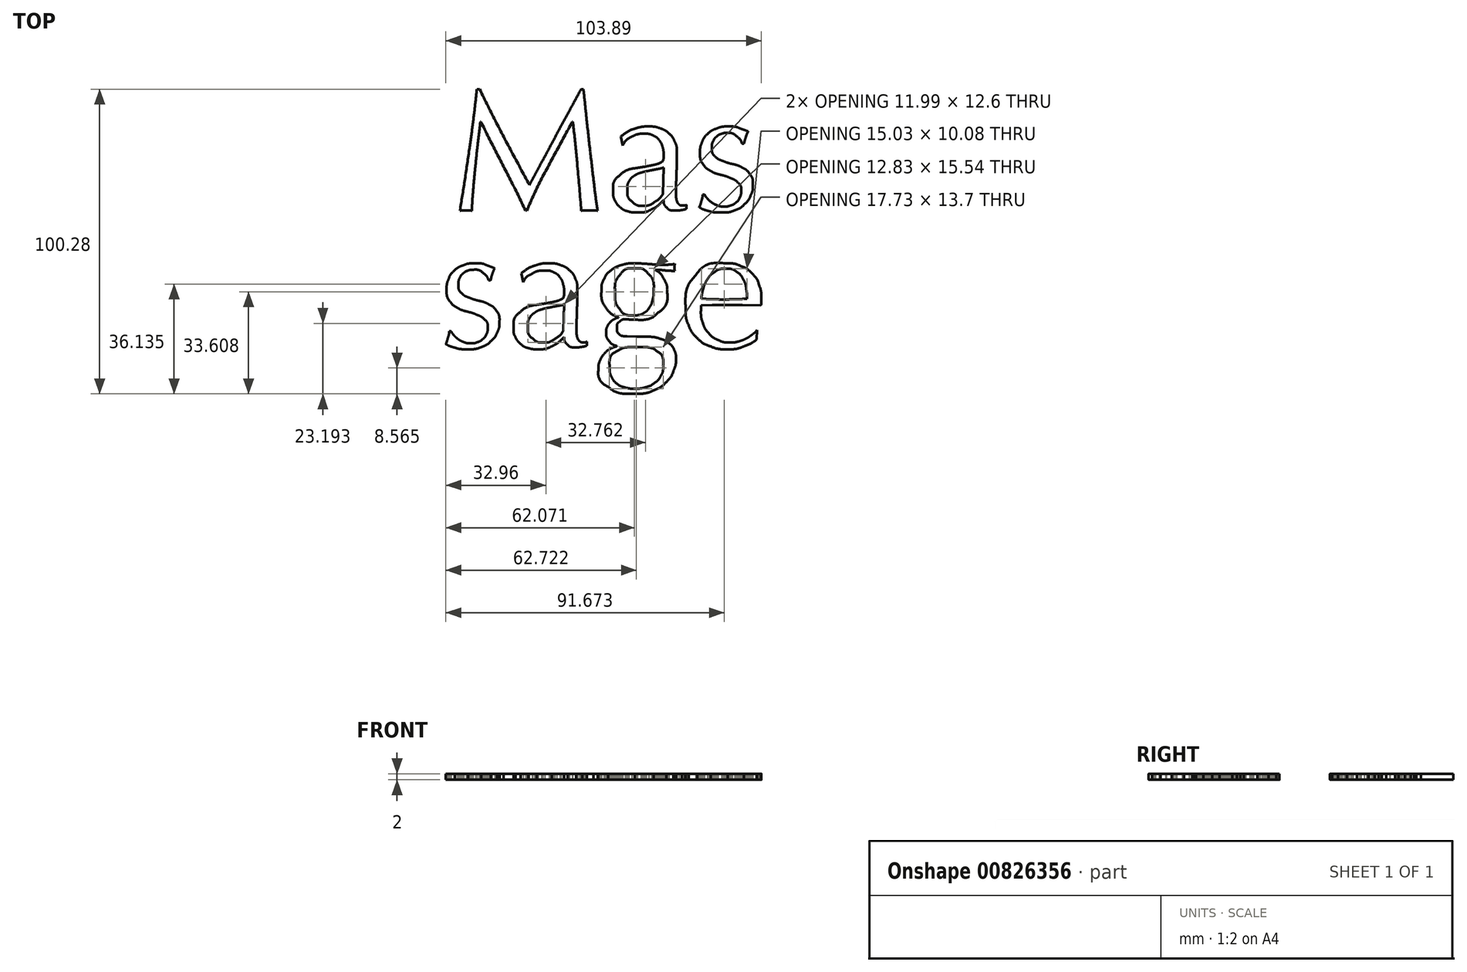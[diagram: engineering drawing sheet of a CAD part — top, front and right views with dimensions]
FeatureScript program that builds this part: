
annotation { "Feature Type Name" : "Feature", "Feature Type Description" : "" }
export const myFeature = defineFeature(function(context is Context, id is Id, definition is map)
    precondition{}
    {
        {
            var Q0;
            Q0=qCreatedBy(makeId("Top.planeOp"),FACE);
            var sketch = newSketch(context, id + "F0", { "sketchPlane" : qUnion([Q0])});
            skFitSpline(sketch, "E0", {"points": [v(-43.66, 49) * mm, v(-43.96, 45.94) * mm, v(-44.33, 42.72) * mm, v(-44.74, 39.33) * mm]});
            skFitSpline(sketch, "E1", {"points": [v(-44.74, 39.33) * mm, v(-45.16, 35.98) * mm, v(-45.62, 32.57) * mm, v(-46.12, 29.1) * mm]});
            skFitSpline(sketch, "E2", {"points": [v(-46.12, 29.1) * mm, v(-46.61, 25.64) * mm, v(-47.13, 22.2) * mm, v(-47.66, 18.76) * mm]});
            skFitSpline(sketch, "E3", {"points": [v(-47.66, 18.76) * mm, v(-48.2, 15.33) * mm, v(-48.7, 12.08) * mm, v(-49.2, 9) * mm]});
            skFitSpline(sketch, "E4", {"points": [v(-49.2, 9) * mm, v(-48.6, 9.07) * mm, v(-47.93, 9.1) * mm, v(-47.2, 9.1) * mm]});
            skFitSpline(sketch, "E5", {"points": [v(-47.2, 9.1) * mm, v(-46.48, 9.1) * mm, v(-45.81, 9.07) * mm, v(-45.2, 9) * mm]});
            skFitSpline(sketch, "E6", {"points": [v(-45.2, 9) * mm, v(-45.2, 10.51) * mm, v(-45.1, 12.46) * mm, v(-44.92, 14.82) * mm]});
            skFitSpline(sketch, "E7", {"points": [v(-44.92, 14.82) * mm, v(-44.73, 17.22) * mm, v(-44.5, 19.75) * mm, v(-44.23, 22.42) * mm]});
            skFitSpline(sketch, "E8", {"points": [v(-44.23, 22.42) * mm, v(-43.96, 25.12) * mm, v(-43.68, 27.85) * mm, v(-43.37, 30.6) * mm]});
            skFitSpline(sketch, "E9", {"points": [v(-43.37, 30.6) * mm, v(-43.03, 33.37) * mm, v(-42.73, 35.94) * mm, v(-42.46, 38.3) * mm]});
            skLineSegment(sketch, "E10", {"start": v(-42.69, 49) * mm, "end": v(-43.66, 49) * mm});
            skLineSegment(sketch, "E11", {"start": v(-43.66, 49) * mm, "end": v(-42.69, 49) * mm});
            skFitSpline(sketch, "E12", {"points": [v(-42.34, 38.3) * mm, v(-39.83, 33.28) * mm, v(-37.33, 28.34) * mm, v(-34.86, 23.5) * mm]});
            skFitSpline(sketch, "E13", {"points": [v(-34.86, 23.5) * mm, v(-32.34, 18.7) * mm, v(-29.94, 13.9) * mm, v(-27.66, 9.1) * mm]});
            skLineSegment(sketch, "E14", {"start": v(-42.46, 38.3) * mm, "end": v(-42.34, 38.3) * mm});
            skLineSegment(sketch, "E15", {"start": v(-42.34, 38.3) * mm, "end": v(-42.46, 38.3) * mm});
            skFitSpline(sketch, "E16", {"points": [v(-27.14, 9.1) * mm, v(-24.86, 14.29) * mm, v(-22.46, 19.24) * mm, v(-19.94, 23.96) * mm]});
            skFitSpline(sketch, "E17", {"points": [v(-19.94, 23.96) * mm, v(-17.4, 28.72) * mm, v(-14.8, 33.5) * mm, v(-12.17, 38.3) * mm]});
            skLineSegment(sketch, "E18", {"start": v(-27.66, 9.1) * mm, "end": v(-27.14, 9.1) * mm});
            skLineSegment(sketch, "E19", {"start": v(-27.14, 9.1) * mm, "end": v(-27.66, 9.1) * mm});
            skFitSpline(sketch, "E20", {"points": [v(-12.06, 38.3) * mm, v(-11.45, 33.35) * mm, v(-10.93, 28.5) * mm, v(-10.52, 23.73) * mm]});
            skFitSpline(sketch, "E21", {"points": [v(-10.52, 23.73) * mm, v(-10.1, 18.97) * mm, v(-9.68, 14.06) * mm, v(-9.26, 9) * mm]});
            skFitSpline(sketch, "E22", {"points": [v(-9.26, 9) * mm, v(-8.8, 9.07) * mm, v(-8.36, 9.1) * mm, v(-7.94, 9.1) * mm]});
            skFitSpline(sketch, "E23", {"points": [v(-7.94, 9.1) * mm, v(-7.49, 9.1) * mm, v(-7.03, 9.1) * mm, v(-6.57, 9.1) * mm]});
            skFitSpline(sketch, "E24", {"points": [v(-6.57, 9.1) * mm, v(-6.12, 9.1) * mm, v(-5.68, 9.1) * mm, v(-5.26, 9.1) * mm]});
            skFitSpline(sketch, "E25", {"points": [v(-5.26, 9.1) * mm, v(-4.8, 9.1) * mm, v(-4.34, 9.07) * mm, v(-3.89, 9) * mm]});
            skFitSpline(sketch, "E26", {"points": [v(-3.89, 9) * mm, v(-4.34, 12.15) * mm, v(-4.76, 15.33) * mm, v(-5.14, 18.53) * mm]});
            skFitSpline(sketch, "E27", {"points": [v(-5.14, 18.53) * mm, v(-5.53, 21.77) * mm, v(-5.9, 25.03) * mm, v(-6.29, 28.3) * mm]});
            skFitSpline(sketch, "E28", {"points": [v(-6.29, 28.3) * mm, v(-6.67, 31.62) * mm, v(-7.05, 34.97) * mm, v(-7.43, 38.36) * mm]});
            skFitSpline(sketch, "E29", {"points": [v(-7.43, 38.36) * mm, v(-7.77, 41.8) * mm, v(-8.15, 45.33) * mm, v(-8.57, 49) * mm]});
            skLineSegment(sketch, "E30", {"start": v(-12.17, 38.3) * mm, "end": v(-12.06, 38.3) * mm});
            skLineSegment(sketch, "E31", {"start": v(-12.06, 38.3) * mm, "end": v(-12.17, 38.3) * mm});
            skFitSpline(sketch, "E32", {"points": [v(-9.32, 49) * mm, v(-10.27, 47.24) * mm, v(-11.3, 45.35) * mm, v(-12.4, 43.33) * mm]});
            skFitSpline(sketch, "E33", {"points": [v(-12.4, 43.33) * mm, v(-13.5, 41.31) * mm, v(-14.63, 39.26) * mm, v(-15.77, 37.16) * mm]});
            skFitSpline(sketch, "E34", {"points": [v(-15.77, 37.16) * mm, v(-16.88, 35.07) * mm, v(-17.98, 33) * mm, v(-19.09, 30.93) * mm]});
            skFitSpline(sketch, "E35", {"points": [v(-19.09, 30.93) * mm, v(-20.15, 28.91) * mm, v(-21.16, 27.03) * mm, v(-22.12, 25.28) * mm]});
            skFitSpline(sketch, "E36", {"points": [v(-22.12, 25.28) * mm, v(-23.07, 23.52) * mm, v(-23.9, 21.96) * mm, v(-24.63, 20.6) * mm]});
            skFitSpline(sketch, "E37", {"points": [v(-24.63, 20.6) * mm, v(-25.35, 19.26) * mm, v(-25.9, 18.23) * mm, v(-26.29, 17.5) * mm]});
            skFitSpline(sketch, "E38", {"points": [v(-26.29, 17.5) * mm, v(-29.22, 22.88) * mm, v(-32.04, 28.11) * mm, v(-34.74, 33.22) * mm]});
            skFitSpline(sketch, "E39", {"points": [v(-34.74, 33.22) * mm, v(-37.41, 38.32) * mm, v(-40.06, 43.58) * mm, v(-42.69, 49) * mm]});
            skLineSegment(sketch, "E40", {"start": v(-8.57, 49) * mm, "end": v(-9.32, 49) * mm});
            skLineSegment(sketch, "E41", {"start": v(-9.32, 49) * mm, "end": v(-8.57, 49) * mm});
            skFitSpline(sketch, "E42", {"points": [v(17.64, 14.65) * mm, v(16.99, 13.58) * mm, v(16.06, 12.65) * mm, v(14.84, 11.85) * mm]});
            skFitSpline(sketch, "E43", {"points": [v(14.84, 11.85) * mm, v(13.66, 11.05) * mm, v(12.34, 10.65) * mm, v(10.9, 10.65) * mm]});
            skFitSpline(sketch, "E44", {"points": [v(10.9, 10.65) * mm, v(9.64, 10.65) * mm, v(8.5, 11.1) * mm, v(7.47, 12.02) * mm]});
            skFitSpline(sketch, "E45", {"points": [v(7.47, 12.02) * mm, v(6.44, 12.93) * mm, v(5.92, 14.29) * mm, v(5.92, 16.08) * mm]});
            skFitSpline(sketch, "E46", {"points": [v(5.92, 16.08) * mm, v(5.92, 17.14) * mm, v(6.11, 18.02) * mm, v(6.5, 18.7) * mm]});
            skFitSpline(sketch, "E47", {"points": [v(6.5, 18.7) * mm, v(6.91, 19.4) * mm, v(7.45, 19.96) * mm, v(8.1, 20.42) * mm]});
            skFitSpline(sketch, "E48", {"points": [v(8.1, 20.42) * mm, v(8.78, 20.88) * mm, v(9.54, 21.24) * mm, v(10.38, 21.5) * mm]});
            skFitSpline(sketch, "E49", {"points": [v(10.38, 21.5) * mm, v(11.26, 21.77) * mm, v(12.13, 21.98) * mm, v(13, 22.13) * mm]});
            skFitSpline(sketch, "E50", {"points": [v(13, 22.13) * mm, v(13.88, 22.32) * mm, v(14.74, 22.5) * mm, v(15.58, 22.65) * mm]});
            skFitSpline(sketch, "E51", {"points": [v(15.58, 22.65) * mm, v(16.46, 22.8) * mm, v(17.22, 23) * mm, v(17.87, 23.22) * mm]});
            skLineSegment(sketch, "E52", {"start": v(17.87, 23.22) * mm, "end": v(17.64, 14.65) * mm});
            skLineSegment(sketch, "E53", {"start": v(17.64, 14.65) * mm, "end": v(17.87, 23.22) * mm});
            skFitSpline(sketch, "E54", {"points": [v(4.38, 30.42) * mm, v(5.03, 31.64) * mm, v(6, 32.6) * mm, v(7.3, 33.28) * mm]});
            skFitSpline(sketch, "E55", {"points": [v(7.3, 33.28) * mm, v(8.63, 33.96) * mm, v(10.06, 34.3) * mm, v(11.58, 34.3) * mm]});
            skFitSpline(sketch, "E56", {"points": [v(11.58, 34.3) * mm, v(12.72, 34.3) * mm, v(13.7, 34.1) * mm, v(14.5, 33.68) * mm]});
            skFitSpline(sketch, "E57", {"points": [v(14.5, 33.68) * mm, v(15.3, 33.3) * mm, v(15.94, 32.78) * mm, v(16.44, 32.13) * mm]});
            skFitSpline(sketch, "E58", {"points": [v(16.44, 32.13) * mm, v(16.93, 31.49) * mm, v(17.3, 30.72) * mm, v(17.52, 29.85) * mm]});
            skFitSpline(sketch, "E59", {"points": [v(17.52, 29.85) * mm, v(17.75, 28.97) * mm, v(17.87, 28.06) * mm, v(17.87, 27.1) * mm]});
            skFitSpline(sketch, "E60", {"points": [v(17.87, 27.1) * mm, v(17.87, 26.53) * mm, v(17.8, 26.06) * mm, v(17.7, 25.68) * mm]});
            skFitSpline(sketch, "E61", {"points": [v(17.7, 25.68) * mm, v(17.58, 25.33) * mm, v(17.24, 25.03) * mm, v(16.67, 24.76) * mm]});
            skFitSpline(sketch, "E62", {"points": [v(16.67, 24.76) * mm, v(16.13, 24.5) * mm, v(15.27, 24.23) * mm, v(14.1, 23.96) * mm]});
            skFitSpline(sketch, "E63", {"points": [v(14.1, 23.96) * mm, v(12.95, 23.73) * mm, v(11.35, 23.45) * mm, v(9.3, 23.1) * mm]});
            skFitSpline(sketch, "E64", {"points": [v(9.3, 23.1) * mm, v(6.78, 22.69) * mm, v(4.8, 21.85) * mm, v(3.35, 20.6) * mm]});
            skFitSpline(sketch, "E65", {"points": [v(3.35, 20.6) * mm, v(1.94, 19.33) * mm, v(1.24, 17.56) * mm, v(1.24, 15.28) * mm]});
            skFitSpline(sketch, "E66", {"points": [v(1.24, 15.28) * mm, v(1.24, 14.17) * mm, v(1.45, 13.18) * mm, v(1.87, 12.3) * mm]});
            skFitSpline(sketch, "E67", {"points": [v(1.87, 12.3) * mm, v(2.32, 11.47) * mm, v(2.9, 10.74) * mm, v(3.58, 10.13) * mm]});
            skFitSpline(sketch, "E68", {"points": [v(3.58, 10.13) * mm, v(4.3, 9.52) * mm, v(5.12, 9.09) * mm, v(6.04, 8.82) * mm]});
            skFitSpline(sketch, "E69", {"points": [v(6.04, 8.82) * mm, v(6.95, 8.55) * mm, v(7.88, 8.42) * mm, v(8.84, 8.42) * mm]});
            skFitSpline(sketch, "E70", {"points": [v(8.84, 8.42) * mm, v(10.78, 8.42) * mm, v(12.42, 8.74) * mm, v(13.75, 9.4) * mm]});
            skFitSpline(sketch, "E71", {"points": [v(13.75, 9.4) * mm, v(15.08, 10.04) * mm, v(16.44, 11.05) * mm, v(17.8, 12.42) * mm]});
            skFitSpline(sketch, "E72", {"points": [v(17.8, 12.42) * mm, v(17.92, 11.43) * mm, v(18.3, 10.6) * mm, v(18.95, 9.96) * mm]});
            skFitSpline(sketch, "E73", {"points": [v(18.95, 9.96) * mm, v(19.6, 9.35) * mm, v(20.53, 9.05) * mm, v(21.75, 9.05) * mm]});
            skFitSpline(sketch, "E74", {"points": [v(21.75, 9.05) * mm, v(22.51, 9.05) * mm, v(23.2, 9.1) * mm, v(23.8, 9.22) * mm]});
            skFitSpline(sketch, "E75", {"points": [v(23.8, 9.22) * mm, v(24.46, 9.33) * mm, v(24.99, 9.49) * mm, v(25.4, 9.68) * mm]});
            skLineSegment(sketch, "E76", {"start": v(3.75, 33.4) * mm, "end": v(3.75, 30.42) * mm});
            skLineSegment(sketch, "E77", {"start": v(3.75, 30.42) * mm, "end": v(4.38, 30.42) * mm});
            skLineSegment(sketch, "E78", {"start": v(4.38, 30.42) * mm, "end": v(3.75, 33.4) * mm});
            skFitSpline(sketch, "E79", {"points": [v(25.4, 10.93) * mm, v(25.22, 10.82) * mm, v(25, 10.74) * mm, v(24.78, 10.7) * mm]});
            skFitSpline(sketch, "E80", {"points": [v(24.78, 10.7) * mm, v(24.59, 10.7) * mm, v(24.4, 10.7) * mm, v(24.2, 10.7) * mm]});
            skFitSpline(sketch, "E81", {"points": [v(24.2, 10.7) * mm, v(23.64, 10.7) * mm, v(23.2, 10.84) * mm, v(22.9, 11.1) * mm]});
            skFitSpline(sketch, "E82", {"points": [v(22.9, 11.1) * mm, v(22.63, 11.37) * mm, v(22.42, 11.7) * mm, v(22.27, 12.08) * mm]});
            skFitSpline(sketch, "E83", {"points": [v(22.27, 12.08) * mm, v(22.11, 12.5) * mm, v(22.02, 12.95) * mm, v(21.98, 13.45) * mm]});
            skFitSpline(sketch, "E84", {"points": [v(21.98, 13.45) * mm, v(21.98, 13.98) * mm, v(21.98, 14.48) * mm, v(21.98, 14.93) * mm]});
            skFitSpline(sketch, "E85", {"points": [v(21.98, 14.93) * mm, v(21.98, 17.33) * mm, v(22.02, 19.6) * mm, v(22.1, 21.73) * mm]});
            skFitSpline(sketch, "E86", {"points": [v(22.1, 21.73) * mm, v(22.17, 23.9) * mm, v(22.2, 26.08) * mm, v(22.2, 28.25) * mm]});
            skFitSpline(sketch, "E87", {"points": [v(22.2, 28.25) * mm, v(22.2, 29.5) * mm, v(21.98, 30.65) * mm, v(21.52, 31.68) * mm]});
            skFitSpline(sketch, "E88", {"points": [v(21.52, 31.68) * mm, v(21.07, 32.74) * mm, v(20.44, 33.64) * mm, v(19.64, 34.36) * mm]});
            skFitSpline(sketch, "E89", {"points": [v(19.64, 34.36) * mm, v(18.84, 35.12) * mm, v(17.87, 35.7) * mm, v(16.72, 36.08) * mm]});
            skFitSpline(sketch, "E90", {"points": [v(16.72, 36.08) * mm, v(15.58, 36.5) * mm, v(14.32, 36.7) * mm, v(12.95, 36.7) * mm]});
            skFitSpline(sketch, "E91", {"points": [v(12.95, 36.7) * mm, v(11.43, 36.7) * mm, v(9.94, 36.48) * mm, v(8.5, 36.02) * mm]});
            skFitSpline(sketch, "E92", {"points": [v(8.5, 36.02) * mm, v(7.05, 35.56) * mm, v(5.47, 34.69) * mm, v(3.75, 33.4) * mm]});
            skLineSegment(sketch, "E93", {"start": v(25.4, 9.68) * mm, "end": v(25.4, 10.93) * mm});
            skLineSegment(sketch, "E94", {"start": v(25.4, 10.93) * mm, "end": v(25.4, 9.68) * mm});
            skFitSpline(sketch, "E95", {"points": [v(30.67, 14.3) * mm, v(30.67, 13.73) * mm, v(30.53, 13) * mm, v(30.27, 12.13) * mm]});
            skFitSpline(sketch, "E96", {"points": [v(30.27, 12.13) * mm, v(30.04, 11.3) * mm, v(29.81, 10.63) * mm, v(29.58, 10.13) * mm]});
            skFitSpline(sketch, "E97", {"points": [v(29.58, 10.13) * mm, v(30.38, 9.68) * mm, v(31.37, 9.28) * mm, v(32.55, 8.93) * mm]});
            skFitSpline(sketch, "E98", {"points": [v(32.55, 8.93) * mm, v(33.73, 8.6) * mm, v(35.2, 8.42) * mm, v(36.95, 8.42) * mm]});
            skFitSpline(sketch, "E99", {"points": [v(36.95, 8.42) * mm, v(38.55, 8.42) * mm, v(39.98, 8.65) * mm, v(41.24, 9.1) * mm]});
            skFitSpline(sketch, "E100", {"points": [v(41.24, 9.1) * mm, v(42.5, 9.6) * mm, v(43.56, 10.27) * mm, v(44.44, 11.1) * mm]});
            skFitSpline(sketch, "E101", {"points": [v(44.44, 11.1) * mm, v(45.35, 11.98) * mm, v(46.04, 12.95) * mm, v(46.5, 14.02) * mm]});
            skFitSpline(sketch, "E102", {"points": [v(46.5, 14.02) * mm, v(47, 15.09) * mm, v(47.24, 16.17) * mm, v(47.24, 17.28) * mm]});
            skFitSpline(sketch, "E103", {"points": [v(47.24, 17.28) * mm, v(47.24, 18.88) * mm, v(46.9, 20.13) * mm, v(46.21, 21.05) * mm]});
            skFitSpline(sketch, "E104", {"points": [v(46.21, 21.05) * mm, v(45.56, 21.96) * mm, v(44.74, 22.67) * mm, v(43.75, 23.16) * mm]});
            skFitSpline(sketch, "E105", {"points": [v(43.75, 23.16) * mm, v(42.76, 23.7) * mm, v(41.68, 24.1) * mm, v(40.5, 24.36) * mm]});
            skFitSpline(sketch, "E106", {"points": [v(40.5, 24.36) * mm, v(39.32, 24.67) * mm, v(38.23, 25) * mm, v(37.24, 25.4) * mm]});
            skFitSpline(sketch, "E107", {"points": [v(37.24, 25.4) * mm, v(36.25, 25.77) * mm, v(35.41, 26.29) * mm, v(34.73, 26.93) * mm]});
            skFitSpline(sketch, "E108", {"points": [v(34.73, 26.93) * mm, v(34.08, 27.62) * mm, v(33.75, 28.57) * mm, v(33.75, 29.8) * mm]});
            skFitSpline(sketch, "E109", {"points": [v(33.75, 29.8) * mm, v(33.75, 30.63) * mm, v(33.9, 31.35) * mm, v(34.21, 31.96) * mm]});
            skFitSpline(sketch, "E110", {"points": [v(34.21, 31.96) * mm, v(34.52, 32.57) * mm, v(34.9, 33.07) * mm, v(35.35, 33.45) * mm]});
            skFitSpline(sketch, "E111", {"points": [v(35.35, 33.45) * mm, v(35.81, 33.83) * mm, v(36.33, 34.11) * mm, v(36.9, 34.3) * mm]});
            skFitSpline(sketch, "E112", {"points": [v(36.9, 34.3) * mm, v(37.47, 34.5) * mm, v(38.04, 34.6) * mm, v(38.61, 34.6) * mm]});
            skFitSpline(sketch, "E113", {"points": [v(38.61, 34.6) * mm, v(39.9, 34.6) * mm, v(41, 34.23) * mm, v(41.87, 33.5) * mm]});
            skFitSpline(sketch, "E114", {"points": [v(41.87, 33.5) * mm, v(42.74, 32.78) * mm, v(43.33, 31.96) * mm, v(43.64, 31.05) * mm]});
            skLineSegment(sketch, "E115", {"start": v(31.35, 14.3) * mm, "end": v(30.67, 14.3) * mm});
            skLineSegment(sketch, "E116", {"start": v(30.67, 14.3) * mm, "end": v(31.35, 14.3) * mm});
            skFitSpline(sketch, "E117", {"points": [v(44.33, 31.05) * mm, v(44.4, 31.5) * mm, v(44.57, 32.15) * mm, v(44.84, 33) * mm]});
            skFitSpline(sketch, "E118", {"points": [v(44.84, 33) * mm, v(45.1, 33.83) * mm, v(45.4, 34.53) * mm, v(45.7, 35.1) * mm]});
            skFitSpline(sketch, "E119", {"points": [v(45.7, 35.1) * mm, v(44.82, 35.4) * mm, v(43.89, 35.75) * mm, v(42.9, 36.13) * mm]});
            skFitSpline(sketch, "E120", {"points": [v(42.9, 36.13) * mm, v(41.94, 36.51) * mm, v(40.76, 36.7) * mm, v(39.35, 36.7) * mm]});
            skFitSpline(sketch, "E121", {"points": [v(39.35, 36.7) * mm, v(37.83, 36.7) * mm, v(36.48, 36.48) * mm, v(35.3, 36.02) * mm]});
            skFitSpline(sketch, "E122", {"points": [v(35.3, 36.02) * mm, v(34.12, 35.6) * mm, v(33.13, 35) * mm, v(32.33, 34.25) * mm]});
            skFitSpline(sketch, "E123", {"points": [v(32.33, 34.25) * mm, v(31.53, 33.49) * mm, v(30.92, 32.57) * mm, v(30.5, 31.5) * mm]});
            skFitSpline(sketch, "E124", {"points": [v(30.5, 31.5) * mm, v(30.08, 30.48) * mm, v(29.87, 29.33) * mm, v(29.87, 28.08) * mm]});
            skFitSpline(sketch, "E125", {"points": [v(29.87, 28.08) * mm, v(29.87, 26.48) * mm, v(30.2, 25.22) * mm, v(30.84, 24.3) * mm]});
            skFitSpline(sketch, "E126", {"points": [v(30.84, 24.3) * mm, v(31.53, 23.4) * mm, v(32.36, 22.65) * mm, v(33.35, 22.08) * mm]});
            skFitSpline(sketch, "E127", {"points": [v(33.35, 22.08) * mm, v(34.34, 21.54) * mm, v(35.43, 21.12) * mm, v(36.61, 20.82) * mm]});
            skFitSpline(sketch, "E128", {"points": [v(36.61, 20.82) * mm, v(37.8, 20.51) * mm, v(38.88, 20.15) * mm, v(39.87, 19.73) * mm]});
            skFitSpline(sketch, "E129", {"points": [v(39.87, 19.73) * mm, v(40.86, 19.35) * mm, v(41.68, 18.84) * mm, v(42.33, 18.2) * mm]});
            skFitSpline(sketch, "E130", {"points": [v(42.33, 18.2) * mm, v(43.01, 17.58) * mm, v(43.35, 16.69) * mm, v(43.35, 15.5) * mm]});
            skFitSpline(sketch, "E131", {"points": [v(43.35, 15.5) * mm, v(43.35, 14.67) * mm, v(43.2, 13.92) * mm, v(42.9, 13.28) * mm]});
            skFitSpline(sketch, "E132", {"points": [v(42.9, 13.28) * mm, v(42.6, 12.63) * mm, v(42.17, 12.1) * mm, v(41.64, 11.68) * mm]});
            skFitSpline(sketch, "E133", {"points": [v(41.64, 11.68) * mm, v(41.14, 11.26) * mm, v(40.55, 10.93) * mm, v(39.87, 10.7) * mm]});
            skFitSpline(sketch, "E134", {"points": [v(39.87, 10.7) * mm, v(39.22, 10.48) * mm, v(38.53, 10.36) * mm, v(37.81, 10.36) * mm]});
            skFitSpline(sketch, "E135", {"points": [v(37.81, 10.36) * mm, v(37.01, 10.36) * mm, v(36.25, 10.5) * mm, v(35.53, 10.76) * mm]});
            skFitSpline(sketch, "E136", {"points": [v(35.53, 10.76) * mm, v(34.84, 11.03) * mm, v(34.21, 11.35) * mm, v(33.64, 11.73) * mm]});
            skFitSpline(sketch, "E137", {"points": [v(33.64, 11.73) * mm, v(33.1, 12.15) * mm, v(32.63, 12.6) * mm, v(32.21, 13.05) * mm]});
            skFitSpline(sketch, "E138", {"points": [v(32.21, 13.05) * mm, v(31.83, 13.5) * mm, v(31.54, 13.92) * mm, v(31.35, 14.3) * mm]});
            skLineSegment(sketch, "E139", {"start": v(43.64, 31.05) * mm, "end": v(44.33, 31.05) * mm});
            skLineSegment(sketch, "E140", {"start": v(44.33, 31.05) * mm, "end": v(43.64, 31.05) * mm});
            skFitSpline(sketch, "E141", {"points": [v(-52.76, -30.7) * mm, v(-52.76, -31.28) * mm, v(-52.9, -32) * mm, v(-53.16, -32.88) * mm]});
            skFitSpline(sketch, "E142", {"points": [v(-53.16, -32.88) * mm, v(-53.4, -33.72) * mm, v(-53.62, -34.39) * mm, v(-53.85, -34.88) * mm]});
            skFitSpline(sketch, "E143", {"points": [v(-53.85, -34.88) * mm, v(-53.05, -35.34) * mm, v(-52.06, -35.74) * mm, v(-50.88, -36.08) * mm]});
            skFitSpline(sketch, "E144", {"points": [v(-50.88, -36.08) * mm, v(-49.7, -36.42) * mm, v(-48.23, -36.6) * mm, v(-46.48, -36.6) * mm]});
            skFitSpline(sketch, "E145", {"points": [v(-46.48, -36.6) * mm, v(-44.88, -36.6) * mm, v(-43.45, -36.37) * mm, v(-42.2, -35.9) * mm]});
            skFitSpline(sketch, "E146", {"points": [v(-42.2, -35.9) * mm, v(-40.94, -35.41) * mm, v(-39.87, -34.75) * mm, v(-39, -33.9) * mm]});
            skFitSpline(sketch, "E147", {"points": [v(-39, -33.9) * mm, v(-38.08, -33.03) * mm, v(-37.4, -32.06) * mm, v(-36.94, -31) * mm]});
            skFitSpline(sketch, "E148", {"points": [v(-36.94, -31) * mm, v(-36.44, -29.93) * mm, v(-36.2, -28.84) * mm, v(-36.2, -27.74) * mm]});
            skFitSpline(sketch, "E149", {"points": [v(-36.2, -27.74) * mm, v(-36.2, -26.14) * mm, v(-36.54, -24.88) * mm, v(-37.22, -23.97) * mm]});
            skFitSpline(sketch, "E150", {"points": [v(-37.22, -23.97) * mm, v(-37.87, -23.05) * mm, v(-38.69, -22.35) * mm, v(-39.68, -21.85) * mm]});
            skFitSpline(sketch, "E151", {"points": [v(-39.68, -21.85) * mm, v(-40.67, -21.32) * mm, v(-41.75, -20.92) * mm, v(-42.94, -20.65) * mm]});
            skFitSpline(sketch, "E152", {"points": [v(-42.94, -20.65) * mm, v(-44.12, -20.35) * mm, v(-45.2, -20) * mm, v(-46.2, -19.62) * mm]});
            skFitSpline(sketch, "E153", {"points": [v(-46.2, -19.62) * mm, v(-47.18, -19.24) * mm, v(-48.02, -18.73) * mm, v(-48.7, -18.08) * mm]});
            skFitSpline(sketch, "E154", {"points": [v(-48.7, -18.08) * mm, v(-49.35, -17.4) * mm, v(-49.68, -16.44) * mm, v(-49.68, -15.22) * mm]});
            skFitSpline(sketch, "E155", {"points": [v(-49.68, -15.22) * mm, v(-49.68, -14.39) * mm, v(-49.53, -13.66) * mm, v(-49.22, -13.05) * mm]});
            skFitSpline(sketch, "E156", {"points": [v(-49.22, -13.05) * mm, v(-48.92, -12.44) * mm, v(-48.54, -11.95) * mm, v(-48.08, -11.57) * mm]});
            skFitSpline(sketch, "E157", {"points": [v(-48.08, -11.57) * mm, v(-47.62, -11.19) * mm, v(-47.1, -10.9) * mm, v(-46.54, -10.7) * mm]});
            skFitSpline(sketch, "E158", {"points": [v(-46.54, -10.7) * mm, v(-45.96, -10.52) * mm, v(-45.4, -10.42) * mm, v(-44.82, -10.42) * mm]});
            skFitSpline(sketch, "E159", {"points": [v(-44.82, -10.42) * mm, v(-43.53, -10.42) * mm, v(-42.44, -10.79) * mm, v(-41.56, -11.5) * mm]});
            skFitSpline(sketch, "E160", {"points": [v(-41.56, -11.5) * mm, v(-40.69, -12.23) * mm, v(-40.1, -13.05) * mm, v(-39.8, -13.97) * mm]});
            skLineSegment(sketch, "E161", {"start": v(-52.08, -30.7) * mm, "end": v(-52.76, -30.7) * mm});
            skLineSegment(sketch, "E162", {"start": v(-52.76, -30.7) * mm, "end": v(-52.08, -30.7) * mm});
            skFitSpline(sketch, "E163", {"points": [v(-39.1, -13.97) * mm, v(-39.03, -13.5) * mm, v(-38.86, -12.86) * mm, v(-38.6, -12.02) * mm]});
            skFitSpline(sketch, "E164", {"points": [v(-38.6, -12.02) * mm, v(-38.33, -11.19) * mm, v(-38.04, -10.48) * mm, v(-37.74, -9.9) * mm]});
            skFitSpline(sketch, "E165", {"points": [v(-37.74, -9.9) * mm, v(-38.61, -9.6) * mm, v(-39.54, -9.26) * mm, v(-40.54, -8.88) * mm]});
            skFitSpline(sketch, "E166", {"points": [v(-40.54, -8.88) * mm, v(-41.49, -8.5) * mm, v(-42.67, -8.3) * mm, v(-44.08, -8.3) * mm]});
            skFitSpline(sketch, "E167", {"points": [v(-44.08, -8.3) * mm, v(-45.6, -8.3) * mm, v(-46.95, -8.54) * mm, v(-48.14, -9) * mm]});
            skFitSpline(sketch, "E168", {"points": [v(-48.14, -9) * mm, v(-49.32, -9.41) * mm, v(-50.3, -10) * mm, v(-51.1, -10.77) * mm]});
            skFitSpline(sketch, "E169", {"points": [v(-51.1, -10.77) * mm, v(-51.9, -11.53) * mm, v(-52.52, -12.44) * mm, v(-52.94, -13.5) * mm]});
            skFitSpline(sketch, "E170", {"points": [v(-52.94, -13.5) * mm, v(-53.35, -14.54) * mm, v(-53.56, -15.68) * mm, v(-53.56, -16.94) * mm]});
            skFitSpline(sketch, "E171", {"points": [v(-53.56, -16.94) * mm, v(-53.56, -18.54) * mm, v(-53.24, -19.8) * mm, v(-52.6, -20.7) * mm]});
            skFitSpline(sketch, "E172", {"points": [v(-52.6, -20.7) * mm, v(-51.9, -21.62) * mm, v(-51.07, -22.37) * mm, v(-50.08, -22.94) * mm]});
            skFitSpline(sketch, "E173", {"points": [v(-50.08, -22.94) * mm, v(-49.09, -23.47) * mm, v(-48, -23.9) * mm, v(-46.82, -24.2) * mm]});
            skFitSpline(sketch, "E174", {"points": [v(-46.82, -24.2) * mm, v(-45.64, -24.5) * mm, v(-44.55, -24.86) * mm, v(-43.56, -25.28) * mm]});
            skFitSpline(sketch, "E175", {"points": [v(-43.56, -25.28) * mm, v(-42.57, -25.66) * mm, v(-41.75, -26.18) * mm, v(-41.1, -26.82) * mm]});
            skFitSpline(sketch, "E176", {"points": [v(-41.1, -26.82) * mm, v(-40.42, -27.43) * mm, v(-40.08, -28.33) * mm, v(-40.08, -29.5) * mm]});
            skFitSpline(sketch, "E177", {"points": [v(-40.08, -29.5) * mm, v(-40.08, -30.35) * mm, v(-40.23, -31.1) * mm, v(-40.54, -31.74) * mm]});
            skFitSpline(sketch, "E178", {"points": [v(-40.54, -31.74) * mm, v(-40.84, -32.39) * mm, v(-41.26, -32.92) * mm, v(-41.8, -33.34) * mm]});
            skFitSpline(sketch, "E179", {"points": [v(-41.8, -33.34) * mm, v(-42.29, -33.76) * mm, v(-42.88, -34.08) * mm, v(-43.56, -34.3) * mm]});
            skFitSpline(sketch, "E180", {"points": [v(-43.56, -34.3) * mm, v(-44.21, -34.54) * mm, v(-44.9, -34.65) * mm, v(-45.62, -34.65) * mm]});
            skFitSpline(sketch, "E181", {"points": [v(-45.62, -34.65) * mm, v(-46.42, -34.65) * mm, v(-47.18, -34.52) * mm, v(-47.9, -34.25) * mm]});
            skFitSpline(sketch, "E182", {"points": [v(-47.9, -34.25) * mm, v(-48.6, -33.99) * mm, v(-49.22, -33.66) * mm, v(-49.8, -33.28) * mm]});
            skFitSpline(sketch, "E183", {"points": [v(-49.8, -33.28) * mm, v(-50.33, -32.86) * mm, v(-50.8, -32.42) * mm, v(-51.22, -31.97) * mm]});
            skFitSpline(sketch, "E184", {"points": [v(-51.22, -31.97) * mm, v(-51.6, -31.5) * mm, v(-51.89, -31.1) * mm, v(-52.08, -30.7) * mm]});
            skLineSegment(sketch, "E185", {"start": v(-39.8, -13.97) * mm, "end": v(-39.1, -13.97) * mm});
            skLineSegment(sketch, "E186", {"start": v(-39.1, -13.97) * mm, "end": v(-39.8, -13.97) * mm});
            skFitSpline(sketch, "E187", {"points": [v(-15.13, -30.37) * mm, v(-15.77, -31.43) * mm, v(-16.7, -32.37) * mm, v(-17.93, -33.17) * mm]});
            skFitSpline(sketch, "E188", {"points": [v(-17.93, -33.17) * mm, v(-19.1, -33.97) * mm, v(-20.42, -34.37) * mm, v(-21.87, -34.37) * mm]});
            skFitSpline(sketch, "E189", {"points": [v(-21.87, -34.37) * mm, v(-23.13, -34.37) * mm, v(-24.27, -33.9) * mm, v(-25.3, -33) * mm]});
            skFitSpline(sketch, "E190", {"points": [v(-25.3, -33) * mm, v(-26.33, -32.08) * mm, v(-26.84, -30.73) * mm, v(-26.84, -28.94) * mm]});
            skFitSpline(sketch, "E191", {"points": [v(-26.84, -28.94) * mm, v(-26.84, -27.87) * mm, v(-26.65, -27) * mm, v(-26.27, -26.3) * mm]});
            skFitSpline(sketch, "E192", {"points": [v(-26.27, -26.3) * mm, v(-25.85, -25.62) * mm, v(-25.32, -25.05) * mm, v(-24.67, -24.6) * mm]});
            skFitSpline(sketch, "E193", {"points": [v(-24.67, -24.6) * mm, v(-23.98, -24.14) * mm, v(-23.22, -23.78) * mm, v(-22.38, -23.5) * mm]});
            skFitSpline(sketch, "E194", {"points": [v(-22.38, -23.5) * mm, v(-21.5, -23.24) * mm, v(-20.63, -23.03) * mm, v(-19.75, -22.88) * mm]});
            skFitSpline(sketch, "E195", {"points": [v(-19.75, -22.88) * mm, v(-18.88, -22.7) * mm, v(-18.02, -22.52) * mm, v(-17.18, -22.37) * mm]});
            skFitSpline(sketch, "E196", {"points": [v(-17.18, -22.37) * mm, v(-16.3, -22.21) * mm, v(-15.54, -22.02) * mm, v(-14.9, -21.8) * mm]});
            skLineSegment(sketch, "E197", {"start": v(-14.9, -21.8) * mm, "end": v(-15.13, -30.37) * mm});
            skLineSegment(sketch, "E198", {"start": v(-15.13, -30.37) * mm, "end": v(-14.9, -21.8) * mm});
            skFitSpline(sketch, "E199", {"points": [v(-28.38, -14.6) * mm, v(-27.74, -13.38) * mm, v(-26.76, -12.42) * mm, v(-25.47, -11.74) * mm]});
            skFitSpline(sketch, "E200", {"points": [v(-25.47, -11.74) * mm, v(-24.14, -11.05) * mm, v(-22.7, -10.7) * mm, v(-21.18, -10.7) * mm]});
            skFitSpline(sketch, "E201", {"points": [v(-21.18, -10.7) * mm, v(-20.04, -10.7) * mm, v(-19.07, -10.92) * mm, v(-18.27, -11.34) * mm]});
            skFitSpline(sketch, "E202", {"points": [v(-18.27, -11.34) * mm, v(-17.47, -11.72) * mm, v(-16.82, -12.23) * mm, v(-16.33, -12.88) * mm]});
            skFitSpline(sketch, "E203", {"points": [v(-16.33, -12.88) * mm, v(-15.83, -13.53) * mm, v(-15.47, -14.3) * mm, v(-15.24, -15.17) * mm]});
            skFitSpline(sketch, "E204", {"points": [v(-15.24, -15.17) * mm, v(-15.01, -16.04) * mm, v(-14.9, -16.96) * mm, v(-14.9, -17.9) * mm]});
            skFitSpline(sketch, "E205", {"points": [v(-14.9, -17.9) * mm, v(-14.9, -18.48) * mm, v(-14.95, -18.96) * mm, v(-15.07, -19.34) * mm]});
            skFitSpline(sketch, "E206", {"points": [v(-15.07, -19.34) * mm, v(-15.18, -19.68) * mm, v(-15.53, -19.99) * mm, v(-16.1, -20.25) * mm]});
            skFitSpline(sketch, "E207", {"points": [v(-16.1, -20.25) * mm, v(-16.63, -20.52) * mm, v(-17.49, -20.79) * mm, v(-18.67, -21.05) * mm]});
            skFitSpline(sketch, "E208", {"points": [v(-18.67, -21.05) * mm, v(-19.81, -21.28) * mm, v(-21.41, -21.57) * mm, v(-23.47, -21.9) * mm]});
            skFitSpline(sketch, "E209", {"points": [v(-23.47, -21.9) * mm, v(-25.98, -22.33) * mm, v(-27.96, -23.17) * mm, v(-29.41, -24.42) * mm]});
            skFitSpline(sketch, "E210", {"points": [v(-29.41, -24.42) * mm, v(-30.82, -25.68) * mm, v(-31.53, -27.45) * mm, v(-31.53, -29.74) * mm]});
            skFitSpline(sketch, "E211", {"points": [v(-31.53, -29.74) * mm, v(-31.53, -30.84) * mm, v(-31.32, -31.83) * mm, v(-30.9, -32.7) * mm]});
            skFitSpline(sketch, "E212", {"points": [v(-30.9, -32.7) * mm, v(-30.44, -33.55) * mm, v(-29.87, -34.27) * mm, v(-29.18, -34.88) * mm]});
            skFitSpline(sketch, "E213", {"points": [v(-29.18, -34.88) * mm, v(-28.46, -35.5) * mm, v(-27.64, -35.93) * mm, v(-26.73, -36.2) * mm]});
            skFitSpline(sketch, "E214", {"points": [v(-26.73, -36.2) * mm, v(-25.81, -36.46) * mm, v(-24.88, -36.6) * mm, v(-23.93, -36.6) * mm]});
            skFitSpline(sketch, "E215", {"points": [v(-23.93, -36.6) * mm, v(-21.98, -36.6) * mm, v(-20.34, -36.27) * mm, v(-19.01, -35.62) * mm]});
            skFitSpline(sketch, "E216", {"points": [v(-19.01, -35.62) * mm, v(-17.68, -34.98) * mm, v(-16.33, -33.97) * mm, v(-14.95, -32.6) * mm]});
            skFitSpline(sketch, "E217", {"points": [v(-14.95, -32.6) * mm, v(-14.84, -33.59) * mm, v(-14.46, -34.4) * mm, v(-13.81, -35.05) * mm]});
            skFitSpline(sketch, "E218", {"points": [v(-13.81, -35.05) * mm, v(-13.16, -35.66) * mm, v(-12.23, -35.97) * mm, v(-11.01, -35.97) * mm]});
            skFitSpline(sketch, "E219", {"points": [v(-11.01, -35.97) * mm, v(-10.25, -35.97) * mm, v(-9.56, -35.9) * mm, v(-8.95, -35.8) * mm]});
            skFitSpline(sketch, "E220", {"points": [v(-8.95, -35.8) * mm, v(-8.3, -35.68) * mm, v(-7.77, -35.53) * mm, v(-7.35, -35.34) * mm]});
            skLineSegment(sketch, "E221", {"start": v(-29.01, -11.62) * mm, "end": v(-29.01, -14.6) * mm});
            skLineSegment(sketch, "E222", {"start": v(-29.01, -14.6) * mm, "end": v(-28.38, -14.6) * mm});
            skLineSegment(sketch, "E223", {"start": v(-28.38, -14.6) * mm, "end": v(-29.01, -11.62) * mm});
            skFitSpline(sketch, "E224", {"points": [v(-7.35, -34.08) * mm, v(-7.54, -34.2) * mm, v(-7.75, -34.27) * mm, v(-7.98, -34.3) * mm]});
            skFitSpline(sketch, "E225", {"points": [v(-7.98, -34.3) * mm, v(-8.17, -34.3) * mm, v(-8.36, -34.3) * mm, v(-8.55, -34.3) * mm]});
            skFitSpline(sketch, "E226", {"points": [v(-8.55, -34.3) * mm, v(-9.13, -34.3) * mm, v(-9.56, -34.18) * mm, v(-9.87, -33.9) * mm]});
            skFitSpline(sketch, "E227", {"points": [v(-9.87, -33.9) * mm, v(-10.14, -33.64) * mm, v(-10.34, -33.32) * mm, v(-10.5, -32.94) * mm]});
            skFitSpline(sketch, "E228", {"points": [v(-10.5, -32.94) * mm, v(-10.65, -32.52) * mm, v(-10.74, -32.06) * mm, v(-10.78, -31.57) * mm]});
            skFitSpline(sketch, "E229", {"points": [v(-10.78, -31.57) * mm, v(-10.78, -31.03) * mm, v(-10.78, -30.54) * mm, v(-10.78, -30.08) * mm]});
            skFitSpline(sketch, "E230", {"points": [v(-10.78, -30.08) * mm, v(-10.78, -27.68) * mm, v(-10.74, -25.41) * mm, v(-10.67, -23.28) * mm]});
            skFitSpline(sketch, "E231", {"points": [v(-10.67, -23.28) * mm, v(-10.6, -21.1) * mm, v(-10.55, -18.94) * mm, v(-10.55, -16.77) * mm]});
            skFitSpline(sketch, "E232", {"points": [v(-10.55, -16.77) * mm, v(-10.55, -15.5) * mm, v(-10.78, -14.37) * mm, v(-11.24, -13.34) * mm]});
            skFitSpline(sketch, "E233", {"points": [v(-11.24, -13.34) * mm, v(-11.7, -12.27) * mm, v(-12.33, -11.38) * mm, v(-13.13, -10.65) * mm]});
            skFitSpline(sketch, "E234", {"points": [v(-13.13, -10.65) * mm, v(-13.93, -9.9) * mm, v(-14.9, -9.32) * mm, v(-16.04, -8.94) * mm]});
            skFitSpline(sketch, "E235", {"points": [v(-16.04, -8.94) * mm, v(-17.18, -8.52) * mm, v(-18.44, -8.3) * mm, v(-19.81, -8.3) * mm]});
            skFitSpline(sketch, "E236", {"points": [v(-19.81, -8.3) * mm, v(-21.34, -8.3) * mm, v(-22.82, -8.54) * mm, v(-24.27, -9) * mm]});
            skFitSpline(sketch, "E237", {"points": [v(-24.27, -9) * mm, v(-25.72, -9.45) * mm, v(-27.3, -10.33) * mm, v(-29.01, -11.62) * mm]});
            skLineSegment(sketch, "E238", {"start": v(-7.35, -35.34) * mm, "end": v(-7.35, -34.08) * mm});
            skLineSegment(sketch, "E239", {"start": v(-7.35, -34.08) * mm, "end": v(-7.35, -35.34) * mm});
            skFitSpline(sketch, "E240", {"points": [v(17.68, -42.08) * mm, v(17.68, -43.38) * mm, v(17.41, -44.48) * mm, v(16.88, -45.4) * mm]});
            skFitSpline(sketch, "E241", {"points": [v(16.88, -45.4) * mm, v(16.34, -46.35) * mm, v(15.64, -47.13) * mm, v(14.76, -47.74) * mm]});
            skFitSpline(sketch, "E242", {"points": [v(14.76, -47.74) * mm, v(13.92, -48.35) * mm, v(12.95, -48.8) * mm, v(11.85, -49.1) * mm]});
            skFitSpline(sketch, "E243", {"points": [v(11.85, -49.1) * mm, v(10.74, -49.41) * mm, v(9.62, -49.57) * mm, v(8.48, -49.57) * mm]});
            skFitSpline(sketch, "E244", {"points": [v(8.48, -49.57) * mm, v(7.3, -49.57) * mm, v(6.2, -49.43) * mm, v(5.16, -49.17) * mm]});
            skFitSpline(sketch, "E245", {"points": [v(5.16, -49.17) * mm, v(4.13, -48.9) * mm, v(3.24, -48.48) * mm, v(2.48, -47.9) * mm]});
            skFitSpline(sketch, "E246", {"points": [v(2.48, -47.9) * mm, v(1.75, -47.34) * mm, v(1.16, -46.6) * mm, v(0.7, -45.68) * mm]});
            skFitSpline(sketch, "E247", {"points": [v(0.7, -45.68) * mm, v(0.29, -44.77) * mm, v(0.08, -43.66) * mm, v(0.08, -42.37) * mm]});
            skFitSpline(sketch, "E248", {"points": [v(0.08, -42.37) * mm, v(0.08, -39.93) * mm, v(0.86, -38.23) * mm, v(2.42, -37.28) * mm]});
            skFitSpline(sketch, "E249", {"points": [v(2.42, -37.28) * mm, v(3.98, -36.37) * mm, v(6.2, -35.9) * mm, v(9.05, -35.9) * mm]});
            skFitSpline(sketch, "E250", {"points": [v(9.05, -35.9) * mm, v(12.13, -35.9) * mm, v(14.34, -36.37) * mm, v(15.68, -37.28) * mm]});
            skFitSpline(sketch, "E251", {"points": [v(15.68, -37.28) * mm, v(17.01, -38.2) * mm, v(17.68, -39.8) * mm, v(17.68, -42.08) * mm]});
            skFitSpline(sketch, "E252", {"points": [v(14.6, -17.34) * mm, v(14.6, -18.4) * mm, v(14.46, -19.43) * mm, v(14.2, -20.42) * mm]});
            skFitSpline(sketch, "E253", {"points": [v(14.2, -20.42) * mm, v(13.96, -21.38) * mm, v(13.58, -22.23) * mm, v(13.05, -23) * mm]});
            skFitSpline(sketch, "E254", {"points": [v(13.05, -23) * mm, v(12.55, -23.72) * mm, v(11.9, -24.3) * mm, v(11.1, -24.77) * mm]});
            skFitSpline(sketch, "E255", {"points": [v(11.1, -24.77) * mm, v(10.34, -25.19) * mm, v(9.41, -25.4) * mm, v(8.3, -25.4) * mm]});
            skFitSpline(sketch, "E256", {"points": [v(8.3, -25.4) * mm, v(6.1, -25.4) * mm, v(4.46, -24.7) * mm, v(3.4, -23.34) * mm]});
            skFitSpline(sketch, "E257", {"points": [v(3.4, -23.34) * mm, v(2.36, -21.93) * mm, v(1.85, -20.02) * mm, v(1.85, -17.62) * mm]});
            skFitSpline(sketch, "E258", {"points": [v(1.85, -17.62) * mm, v(1.85, -15.3) * mm, v(2.42, -13.45) * mm, v(3.56, -12.08) * mm]});
            skFitSpline(sketch, "E259", {"points": [v(3.56, -12.08) * mm, v(4.7, -10.67) * mm, v(6.3, -9.97) * mm, v(8.36, -9.97) * mm]});
            skFitSpline(sketch, "E260", {"points": [v(8.36, -9.97) * mm, v(10.23, -9.97) * mm, v(11.73, -10.6) * mm, v(12.88, -11.85) * mm]});
            skFitSpline(sketch, "E261", {"points": [v(12.88, -11.85) * mm, v(14.02, -13.1) * mm, v(14.6, -14.94) * mm, v(14.6, -17.34) * mm]});
            skFitSpline(sketch, "E262", {"points": [v(-2.6, -17.62) * mm, v(-2.6, -19.72) * mm, v(-2.11, -21.47) * mm, v(-1.12, -22.88) * mm]});
            skFitSpline(sketch, "E263", {"points": [v(-1.12, -22.88) * mm, v(-0.13, -24.25) * mm, v(1.24, -25.32) * mm, v(3, -26.08) * mm]});
            skFitSpline(sketch, "E264", {"points": [v(3, -26.2) * mm, v(2.53, -26.27) * mm, v(2.06, -26.44) * mm, v(1.56, -26.7) * mm]});
            skFitSpline(sketch, "E265", {"points": [v(1.56, -26.7) * mm, v(1.07, -26.98) * mm, v(0.63, -27.32) * mm, v(0.25, -27.74) * mm]});
            skFitSpline(sketch, "E266", {"points": [v(0.25, -27.74) * mm, v(-0.13, -28.16) * mm, v(-0.46, -28.63) * mm, v(-0.72, -29.17) * mm]});
            skFitSpline(sketch, "E267", {"points": [v(-0.72, -29.17) * mm, v(-0.95, -29.7) * mm, v(-1.07, -30.3) * mm, v(-1.07, -30.94) * mm]});
            skFitSpline(sketch, "E268", {"points": [v(-1.07, -30.94) * mm, v(-1.07, -32.04) * mm, v(-0.76, -33) * mm, v(-0.15, -33.8) * mm]});
            skFitSpline(sketch, "E269", {"points": [v(-0.15, -33.8) * mm, v(0.46, -34.6) * mm, v(1.35, -35.17) * mm, v(2.53, -35.5) * mm]});
            skLineSegment(sketch, "E270", {"start": v(3, -26.08) * mm, "end": v(3, -26.2) * mm});
            skLineSegment(sketch, "E271", {"start": v(3, -26.2) * mm, "end": v(3, -26.08) * mm});
            skFitSpline(sketch, "E272", {"points": [v(2.53, -35.62) * mm, v(1.77, -35.81) * mm, v(1.03, -36.1) * mm, v(0.3, -36.48) * mm]});
            skFitSpline(sketch, "E273", {"points": [v(0.3, -36.48) * mm, v(-0.42, -36.86) * mm, v(-1.07, -37.38) * mm, v(-1.64, -38.02) * mm]});
            skFitSpline(sketch, "E274", {"points": [v(-1.64, -38.02) * mm, v(-2.2, -38.67) * mm, v(-2.68, -39.41) * mm, v(-3.07, -40.25) * mm]});
            skFitSpline(sketch, "E275", {"points": [v(-3.07, -40.25) * mm, v(-3.4, -41.1) * mm, v(-3.58, -42) * mm, v(-3.58, -43) * mm]});
            skFitSpline(sketch, "E276", {"points": [v(-3.58, -43) * mm, v(-3.58, -45.55) * mm, v(-2.51, -47.55) * mm, v(-0.38, -49) * mm]});
            skFitSpline(sketch, "E277", {"points": [v(-0.38, -49) * mm, v(1.75, -50.48) * mm, v(4.67, -51.22) * mm, v(8.36, -51.22) * mm]});
            skFitSpline(sketch, "E278", {"points": [v(8.36, -51.22) * mm, v(10.76, -51.22) * mm, v(12.82, -50.86) * mm, v(14.53, -50.14) * mm]});
            skFitSpline(sketch, "E279", {"points": [v(14.53, -50.14) * mm, v(16.25, -49.41) * mm, v(17.64, -48.5) * mm, v(18.7, -47.4) * mm]});
            skFitSpline(sketch, "E280", {"points": [v(18.7, -47.4) * mm, v(19.81, -46.3) * mm, v(20.61, -45.05) * mm, v(21.1, -43.68) * mm]});
            skFitSpline(sketch, "E281", {"points": [v(21.1, -43.68) * mm, v(21.64, -42.3) * mm, v(21.9, -40.96) * mm, v(21.9, -39.62) * mm]});
            skFitSpline(sketch, "E282", {"points": [v(21.9, -39.62) * mm, v(21.9, -38.63) * mm, v(21.72, -37.72) * mm, v(21.33, -36.88) * mm]});
            skFitSpline(sketch, "E283", {"points": [v(21.33, -36.88) * mm, v(21, -36.04) * mm, v(20.42, -35.3) * mm, v(19.62, -34.65) * mm]});
            skFitSpline(sketch, "E284", {"points": [v(19.62, -34.65) * mm, v(18.86, -34) * mm, v(17.85, -33.5) * mm, v(16.6, -33.1) * mm]});
            skFitSpline(sketch, "E285", {"points": [v(16.6, -33.1) * mm, v(15.37, -32.73) * mm, v(13.89, -32.52) * mm, v(12.13, -32.48) * mm]});
            skFitSpline(sketch, "E286", {"points": [v(12.13, -32.48) * mm, v(11.07, -32.44) * mm, v(10.02, -32.42) * mm, v(9, -32.42) * mm]});
            skFitSpline(sketch, "E287", {"points": [v(9, -32.42) * mm, v(7.96, -32.39) * mm, v(6.92, -32.35) * mm, v(5.85, -32.3) * mm]});
            skFitSpline(sketch, "E288", {"points": [v(5.85, -32.3) * mm, v(4.55, -32.27) * mm, v(3.66, -32.02) * mm, v(3.16, -31.57) * mm]});
            skFitSpline(sketch, "E289", {"points": [v(3.16, -31.57) * mm, v(2.7, -31.1) * mm, v(2.48, -30.39) * mm, v(2.48, -29.4) * mm]});
            skFitSpline(sketch, "E290", {"points": [v(2.48, -29.4) * mm, v(2.48, -28.63) * mm, v(2.76, -28) * mm, v(3.33, -27.5) * mm]});
            skFitSpline(sketch, "E291", {"points": [v(3.33, -27.5) * mm, v(3.94, -27.01) * mm, v(4.6, -26.77) * mm, v(5.28, -26.77) * mm]});
            skFitSpline(sketch, "E292", {"points": [v(5.28, -26.77) * mm, v(5.81, -26.77) * mm, v(6.32, -26.79) * mm, v(6.82, -26.82) * mm]});
            skFitSpline(sketch, "E293", {"points": [v(6.82, -26.82) * mm, v(7.35, -26.86) * mm, v(7.89, -26.88) * mm, v(8.42, -26.88) * mm]});
            skFitSpline(sketch, "E294", {"points": [v(8.42, -26.88) * mm, v(11.66, -26.88) * mm, v(14.23, -26.08) * mm, v(16.13, -24.48) * mm]});
            skFitSpline(sketch, "E295", {"points": [v(16.13, -24.48) * mm, v(18.08, -22.84) * mm, v(19.05, -20.6) * mm, v(19.05, -17.74) * mm]});
            skFitSpline(sketch, "E296", {"points": [v(19.05, -17.74) * mm, v(19.05, -16.3) * mm, v(18.69, -14.9) * mm, v(17.96, -13.57) * mm]});
            skFitSpline(sketch, "E297", {"points": [v(17.96, -13.57) * mm, v(17.24, -12.2) * mm, v(16.29, -11.19) * mm, v(15.1, -10.54) * mm]});
            skLineSegment(sketch, "E298", {"start": v(2.53, -35.5) * mm, "end": v(2.53, -35.62) * mm});
            skLineSegment(sketch, "E299", {"start": v(2.53, -35.62) * mm, "end": v(2.53, -35.5) * mm});
            skFitSpline(sketch, "E300", {"points": [v(15.22, -10.42) * mm, v(16.25, -10.46) * mm, v(17.28, -10.54) * mm, v(18.3, -10.65) * mm]});
            skFitSpline(sketch, "E301", {"points": [v(18.3, -10.65) * mm, v(19.37, -10.73) * mm, v(20.46, -10.8) * mm, v(21.56, -10.88) * mm]});
            skFitSpline(sketch, "E302", {"points": [v(21.56, -10.88) * mm, v(21.52, -10.7) * mm, v(21.49, -10.5) * mm, v(21.45, -10.3) * mm]});
            skFitSpline(sketch, "E303", {"points": [v(21.45, -10.3) * mm, v(21.45, -10.08) * mm, v(21.45, -9.87) * mm, v(21.45, -9.68) * mm]});
            skFitSpline(sketch, "E304", {"points": [v(21.45, -9.68) * mm, v(21.45, -9.5) * mm, v(21.45, -9.3) * mm, v(21.45, -9.1) * mm]});
            skFitSpline(sketch, "E305", {"points": [v(21.45, -9.1) * mm, v(21.49, -8.88) * mm, v(21.52, -8.67) * mm, v(21.56, -8.48) * mm]});
            skFitSpline(sketch, "E306", {"points": [v(21.56, -8.48) * mm, v(20.61, -8.67) * mm, v(19.07, -8.77) * mm, v(16.93, -8.77) * mm]});
            skFitSpline(sketch, "E307", {"points": [v(16.93, -8.77) * mm, v(16.52, -8.77) * mm, v(15.96, -8.75) * mm, v(15.28, -8.7) * mm]});
            skFitSpline(sketch, "E308", {"points": [v(15.28, -8.7) * mm, v(14.6, -8.67) * mm, v(13.81, -8.61) * mm, v(12.93, -8.54) * mm]});
            skFitSpline(sketch, "E309", {"points": [v(12.93, -8.54) * mm, v(11.9, -8.46) * mm, v(11.05, -8.4) * mm, v(10.36, -8.37) * mm]});
            skFitSpline(sketch, "E310", {"points": [v(10.36, -8.37) * mm, v(9.72, -8.33) * mm, v(9.03, -8.3) * mm, v(8.3, -8.3) * mm]});
            skFitSpline(sketch, "E311", {"points": [v(8.3, -8.3) * mm, v(6.82, -8.3) * mm, v(5.41, -8.5) * mm, v(4.08, -8.88) * mm]});
            skFitSpline(sketch, "E312", {"points": [v(4.08, -8.88) * mm, v(2.78, -9.26) * mm, v(1.62, -9.83) * mm, v(0.6, -10.6) * mm]});
            skFitSpline(sketch, "E313", {"points": [v(0.6, -10.6) * mm, v(-0.4, -11.36) * mm, v(-1.18, -12.33) * mm, v(-1.75, -13.5) * mm]});
            skFitSpline(sketch, "E314", {"points": [v(-1.75, -13.5) * mm, v(-2.32, -14.65) * mm, v(-2.6, -16.02) * mm, v(-2.6, -17.62) * mm]});
            skLineSegment(sketch, "E315", {"start": v(15.1, -10.54) * mm, "end": v(15.22, -10.42) * mm});
            skLineSegment(sketch, "E316", {"start": v(15.22, -10.42) * mm, "end": v(15.1, -10.54) * mm});
            skFitSpline(sketch, "E317", {"points": [v(38.3, -10.14) * mm, v(39.8, -10.14) * mm, v(41, -10.46) * mm, v(41.9, -11.1) * mm]});
            skFitSpline(sketch, "E318", {"points": [v(41.9, -11.1) * mm, v(42.82, -11.76) * mm, v(43.52, -12.58) * mm, v(44.02, -13.57) * mm]});
            skFitSpline(sketch, "E319", {"points": [v(44.02, -13.57) * mm, v(44.55, -14.56) * mm, v(44.9, -15.62) * mm, v(45.05, -16.77) * mm]});
            skFitSpline(sketch, "E320", {"points": [v(45.05, -16.77) * mm, v(45.24, -17.9) * mm, v(45.33, -19) * mm, v(45.33, -20.02) * mm]});
            skFitSpline(sketch, "E321", {"points": [v(45.33, -20.02) * mm, v(44.12, -20.06) * mm, v(42.86, -20.1) * mm, v(41.56, -20.14) * mm]});
            skFitSpline(sketch, "E322", {"points": [v(41.56, -20.14) * mm, v(40.27, -20.18) * mm, v(39, -20.2) * mm, v(37.73, -20.2) * mm]});
            skFitSpline(sketch, "E323", {"points": [v(37.73, -20.2) * mm, v(36.52, -20.2) * mm, v(35.26, -20.18) * mm, v(33.96, -20.14) * mm]});
            skFitSpline(sketch, "E324", {"points": [v(33.96, -20.14) * mm, v(32.7, -20.1) * mm, v(31.49, -20.06) * mm, v(30.3, -20.02) * mm]});
            skFitSpline(sketch, "E325", {"points": [v(30.3, -20.02) * mm, v(30.38, -19) * mm, v(30.57, -17.9) * mm, v(30.88, -16.77) * mm]});
            skFitSpline(sketch, "E326", {"points": [v(30.88, -16.77) * mm, v(31.22, -15.59) * mm, v(31.7, -14.52) * mm, v(32.3, -13.57) * mm]});
            skFitSpline(sketch, "E327", {"points": [v(32.3, -13.57) * mm, v(32.95, -12.58) * mm, v(33.75, -11.76) * mm, v(34.7, -11.1) * mm]});
            skFitSpline(sketch, "E328", {"points": [v(34.7, -11.1) * mm, v(35.7, -10.46) * mm, v(36.9, -10.14) * mm, v(38.3, -10.14) * mm]});
            skFitSpline(sketch, "E329", {"points": [v(25.1, -23.34) * mm, v(25.1, -25.24) * mm, v(25.43, -27.01) * mm, v(26.08, -28.65) * mm]});
            skFitSpline(sketch, "E330", {"points": [v(26.08, -28.65) * mm, v(26.76, -30.3) * mm, v(27.72, -31.72) * mm, v(28.93, -32.94) * mm]});
            skFitSpline(sketch, "E331", {"points": [v(28.93, -32.94) * mm, v(30.2, -34.12) * mm, v(31.66, -35.03) * mm, v(33.33, -35.68) * mm]});
            skFitSpline(sketch, "E332", {"points": [v(33.33, -35.68) * mm, v(35.05, -36.3) * mm, v(36.93, -36.6) * mm, v(39, -36.6) * mm]});
            skFitSpline(sketch, "E333", {"points": [v(39, -36.6) * mm, v(40.82, -36.6) * mm, v(42.57, -36.27) * mm, v(44.25, -35.62) * mm]});
            skFitSpline(sketch, "E334", {"points": [v(44.25, -35.62) * mm, v(45.96, -34.98) * mm, v(47.4, -34.2) * mm, v(48.53, -33.28) * mm]});
            skFitSpline(sketch, "E335", {"points": [v(48.6, -30.3) * mm, v(48.1, -30.88) * mm, v(47.5, -31.41) * mm, v(46.82, -31.9) * mm]});
            skFitSpline(sketch, "E336", {"points": [v(46.82, -31.9) * mm, v(46.17, -32.4) * mm, v(45.47, -32.84) * mm, v(44.7, -33.22) * mm]});
            skFitSpline(sketch, "E337", {"points": [v(44.7, -33.22) * mm, v(43.94, -33.57) * mm, v(43.16, -33.85) * mm, v(42.36, -34.08) * mm]});
            skFitSpline(sketch, "E338", {"points": [v(42.36, -34.08) * mm, v(41.56, -34.27) * mm, v(40.78, -34.37) * mm, v(40.02, -34.37) * mm]});
            skFitSpline(sketch, "E339", {"points": [v(40.02, -34.37) * mm, v(38.42, -34.37) * mm, v(37.01, -34.1) * mm, v(35.8, -33.57) * mm]});
            skFitSpline(sketch, "E340", {"points": [v(35.8, -33.57) * mm, v(34.57, -33) * mm, v(33.54, -32.25) * mm, v(32.7, -31.34) * mm]});
            skFitSpline(sketch, "E341", {"points": [v(32.7, -31.34) * mm, v(31.87, -30.39) * mm, v(31.22, -29.26) * mm, v(30.76, -27.97) * mm]});
            skFitSpline(sketch, "E342", {"points": [v(30.76, -27.97) * mm, v(30.34, -26.67) * mm, v(30.13, -25.28) * mm, v(30.13, -23.8) * mm]});
            skLineSegment(sketch, "E343", {"start": v(48.53, -33.28) * mm, "end": v(48.88, -30.48) * mm});
            skLineSegment(sketch, "E344", {"start": v(48.88, -30.48) * mm, "end": v(48.6, -30.3) * mm});
            skLineSegment(sketch, "E345", {"start": v(48.6, -30.3) * mm, "end": v(48.53, -33.28) * mm});
            skFitSpline(sketch, "E346", {"points": [v(30.13, -23.05) * mm, v(30.13, -22.67) * mm, v(30.15, -22.39) * mm, v(30.2, -22.2) * mm]});
            skFitSpline(sketch, "E347", {"points": [v(30.2, -22.2) * mm, v(31.45, -22.16) * mm, v(32.69, -22.12) * mm, v(33.9, -22.08) * mm]});
            skFitSpline(sketch, "E348", {"points": [v(33.9, -22.08) * mm, v(35.16, -22.04) * mm, v(36.42, -22.02) * mm, v(37.68, -22.02) * mm]});
            skFitSpline(sketch, "E349", {"points": [v(37.68, -22.02) * mm, v(39.73, -22.02) * mm, v(41.77, -22.04) * mm, v(43.8, -22.08) * mm]});
            skFitSpline(sketch, "E350", {"points": [v(43.8, -22.08) * mm, v(45.81, -22.12) * mm, v(47.85, -22.16) * mm, v(49.9, -22.2) * mm]});
            skFitSpline(sketch, "E351", {"points": [v(49.9, -22.2) * mm, v(49.94, -21.81) * mm, v(49.96, -21.45) * mm, v(49.96, -21.1) * mm]});
            skFitSpline(sketch, "E352", {"points": [v(49.96, -21.1) * mm, v(50, -20.73) * mm, v(50.02, -20.35) * mm, v(50.02, -19.97) * mm]});
            skFitSpline(sketch, "E353", {"points": [v(50.02, -19.97) * mm, v(50.02, -18.37) * mm, v(49.77, -16.86) * mm, v(49.28, -15.45) * mm]});
            skFitSpline(sketch, "E354", {"points": [v(49.28, -15.45) * mm, v(48.82, -14.04) * mm, v(48.1, -12.82) * mm, v(47.1, -11.8) * mm]});
            skFitSpline(sketch, "E355", {"points": [v(47.1, -11.8) * mm, v(46.12, -10.73) * mm, v(44.88, -9.9) * mm, v(43.4, -9.28) * mm]});
            skFitSpline(sketch, "E356", {"points": [v(43.4, -9.28) * mm, v(41.94, -8.63) * mm, v(40.21, -8.3) * mm, v(38.2, -8.3) * mm]});
            skFitSpline(sketch, "E357", {"points": [v(38.2, -8.3) * mm, v(33.92, -8.3) * mm, v(30.67, -9.64) * mm, v(28.42, -12.3) * mm]});
            skFitSpline(sketch, "E358", {"points": [v(28.42, -12.3) * mm, v(26.21, -14.98) * mm, v(25.1, -18.65) * mm, v(25.1, -23.34) * mm]});
            skLineSegment(sketch, "E359", {"start": v(30.13, -23.8) * mm, "end": v(30.13, -23.05) * mm});
            skLineSegment(sketch, "E360", {"start": v(30.13, -23.05) * mm, "end": v(30.13, -23.8) * mm});
            skSolve(sketch);
        }
        {
            var Q0;
            Q0=makeQuery(id+"F0.imprint","IMPRINT",FACE,{"disambiguationData":[TD([[makeQuery(id+"F0.imprint","IMPRINT",EDGE,{"derivedFrom":sQuery(id+"F0.wireOp",EDGE,"E0")}),1.0]])]});
            var Q1;
            Q1=makeQuery(id+"F0.imprint","IMPRINT",FACE,{"disambiguationData":[TD([[makeQuery(id+"F0.imprint","IMPRINT",EDGE,{"derivedFrom":sQuery(id+"F0.wireOp",EDGE,"E42")}),1.0]])]});
            var Q2;
            Q2=makeQuery(id+"F0.imprint","IMPRINT",FACE,{"disambiguationData":[TD([[makeQuery(id+"F0.imprint","IMPRINT",EDGE,{"derivedFrom":sQuery(id+"F0.wireOp",EDGE,"E95")}),1.0]])]});
            var Q3;
            Q3=makeQuery(id+"F0.imprint","IMPRINT",FACE,{"disambiguationData":[TD([[makeQuery(id+"F0.imprint","IMPRINT",EDGE,{"derivedFrom":sQuery(id+"F0.wireOp",EDGE,"E317")}),1.0]])]});
            var Q4;
            Q4=makeQuery(id+"F0.imprint","IMPRINT",FACE,{"disambiguationData":[TD([[makeQuery(id+"F0.imprint","IMPRINT",EDGE,{"derivedFrom":sQuery(id+"F0.wireOp",EDGE,"E240")}),1.0]])]});
            var Q5;
            Q5=makeQuery(id+"F0.imprint","IMPRINT",FACE,{"disambiguationData":[TD([[makeQuery(id+"F0.imprint","IMPRINT",EDGE,{"derivedFrom":sQuery(id+"F0.wireOp",EDGE,"E187")}),1.0]])]});
            var Q6;
            Q6=makeQuery(id+"F0.imprint","IMPRINT",FACE,{"disambiguationData":[TD([[makeQuery(id+"F0.imprint","IMPRINT",EDGE,{"derivedFrom":sQuery(id+"F0.wireOp",EDGE,"E141")}),1.0]])]});
            extrude(context, id + "F1", {"entities" : qUnion([Q0, Q1, Q2, Q3, Q4, Q5, Q6]), "depth" : 2 * mm, "offsetDistance" : 25 * mm});
        }
    });
